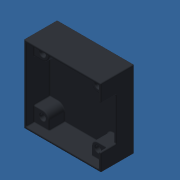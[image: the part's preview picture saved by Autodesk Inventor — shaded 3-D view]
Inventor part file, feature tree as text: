
AUTODESK INVENTOR PART (.ipt)
format: ipt  version: 2018.2 (Build 222227000, 227)  size: 517,120 bytes
history: native  units: in
note: dims shown in document units (in); Inventor stores cm internally (conversion verified against a paired STEP export)
features: extrude x6, sketch x5, hole x2, fillet x2, projected_geometry x1
ambient origin geometry x8: Origin, YZ Plane, XZ Plane, XY Plane, X Axis, Y Axis, Z Axis, Center Point
bodies: Solid1 (feature_tree)
feature tree (16):
  sketch  "Sketch1"  dims[d0=0.8819in d1=0.8819in]
  extrude  "Extrusion1"  Depth=0.8819in
  extrude  "Extrusion2"  Depth=1.1417in
  extrude  "Extrusion3"  Depth=0.0079in
  sketch  "Sketch2"  dims[d2=1.1417in d3=1.1417in]
  hole  "Hole1"  [1 undecoded]
  extrude  "Extrusion5"  Depth=0.16in TaperAngle=0.0deg
  extrude  "Extrusion4"  Depth=0.375in TaperAngle=0.0deg
  extrude  "Extrusion6"  Depth=0.25in TaperAngle=0.0deg
  hole  "Hole2"  [1 undecoded]
  fillet  "Fillet1"  Radius=0.125in
  fillet  "Fillet2"  Radius=0.16in
  sketch  "Sketch3"  dims[d4=0.0079in d5=0.0079in]
  projected_geometry  "Projected Loop1"
  sketch  "Sketch4"  dims[d6=0.0394in d7=0.0394in]
  sketch  "Sketch5"  dims[d8=0.1in d9=0.16in d10=0.0in d11=0.375in d12=0.0in d13=0.25in d14=0.0in d15=0.0866in d16=0.75in d17=0.375in d18=0.25in d19=0.5635in d20=1.0in d21=0.8108in d22=0.1181in d23=0.125in d24=0.0in d25=0.16in d26=0.16in d27=0.08in d28=0.0in d29=0.175in d30=0.175in d31=60.0deg d32=0.375in d33=0.0in d34=0.129in d35=0.75in d36=0.219in d37=0.112in d38=0.5635in d39=1.0in d40=0.8108in d41=0.125in d42=0.016in d43=0.016in]
note: 2 required parameter values undecoded (feature->parameter linkage not recoverable at this tier; creation-order binding heuristic only, values carry confidence <= 0.55)
